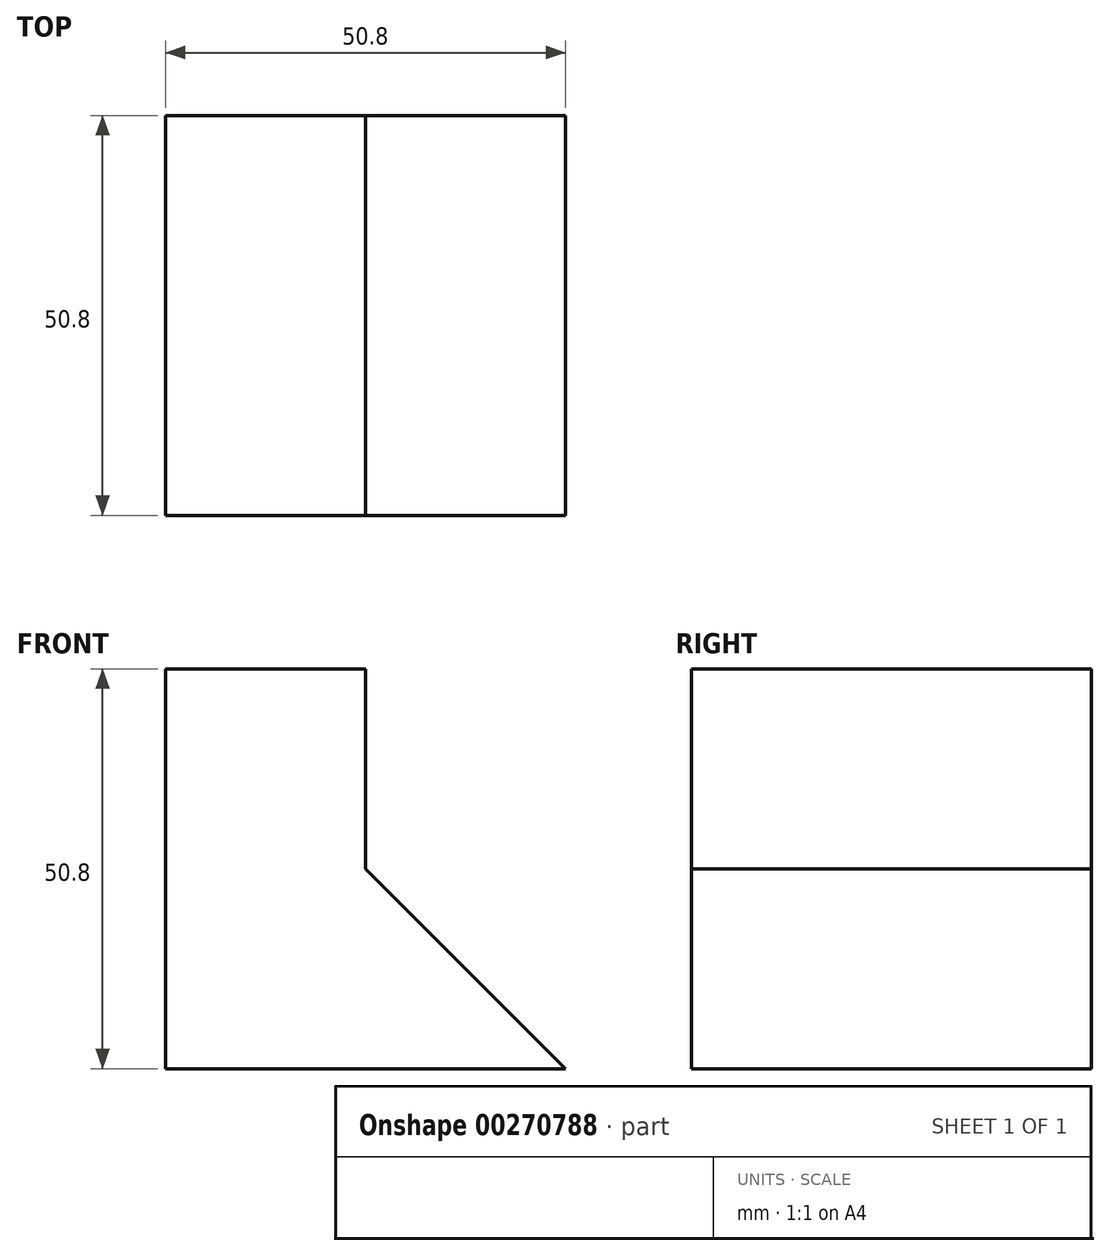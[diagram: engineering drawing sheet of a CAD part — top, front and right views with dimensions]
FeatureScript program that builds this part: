
annotation { "Feature Type Name" : "Feature", "Feature Type Description" : "" }
export const myFeature = defineFeature(function(context is Context, id is Id, definition is map)
    precondition{}
    {
        {
            var Q0;
            Q0=qCreatedBy(makeId("Front.planeOp"),FACE);
            var sketch = newSketch(context, id + "F0", { "sketchPlane" : qUnion([Q0])});
            skLineSegment(sketch, "E0", {"start": v(-47.17, 35.71) * mm, "end": v(-47.17, -15.09) * mm});
            skLineSegment(sketch, "E1", {"start": v(-47.17, -15.09) * mm, "end": v(3.63, -15.09) * mm});
            skLineSegment(sketch, "E2", {"start": v(-47.17, 35.71) * mm, "end": v(-21.77, 35.71) * mm});
            skLineSegment(sketch, "E3", {"start": v(-21.77, 35.71) * mm, "end": v(-21.77, 10.31) * mm});
            skLineSegment(sketch, "E4", {"start": v(-21.77, 10.31) * mm, "end": v(3.63, -15.09) * mm});
            skSolve(sketch);
        }
        {
            var Q0;
            Q0 = qSketchRegion(id + "F0", true);
            extrude(context, id + "F1", {"entities" : qUnion([Q0]), "depth" : 50.8 * mm});
        }
    });
